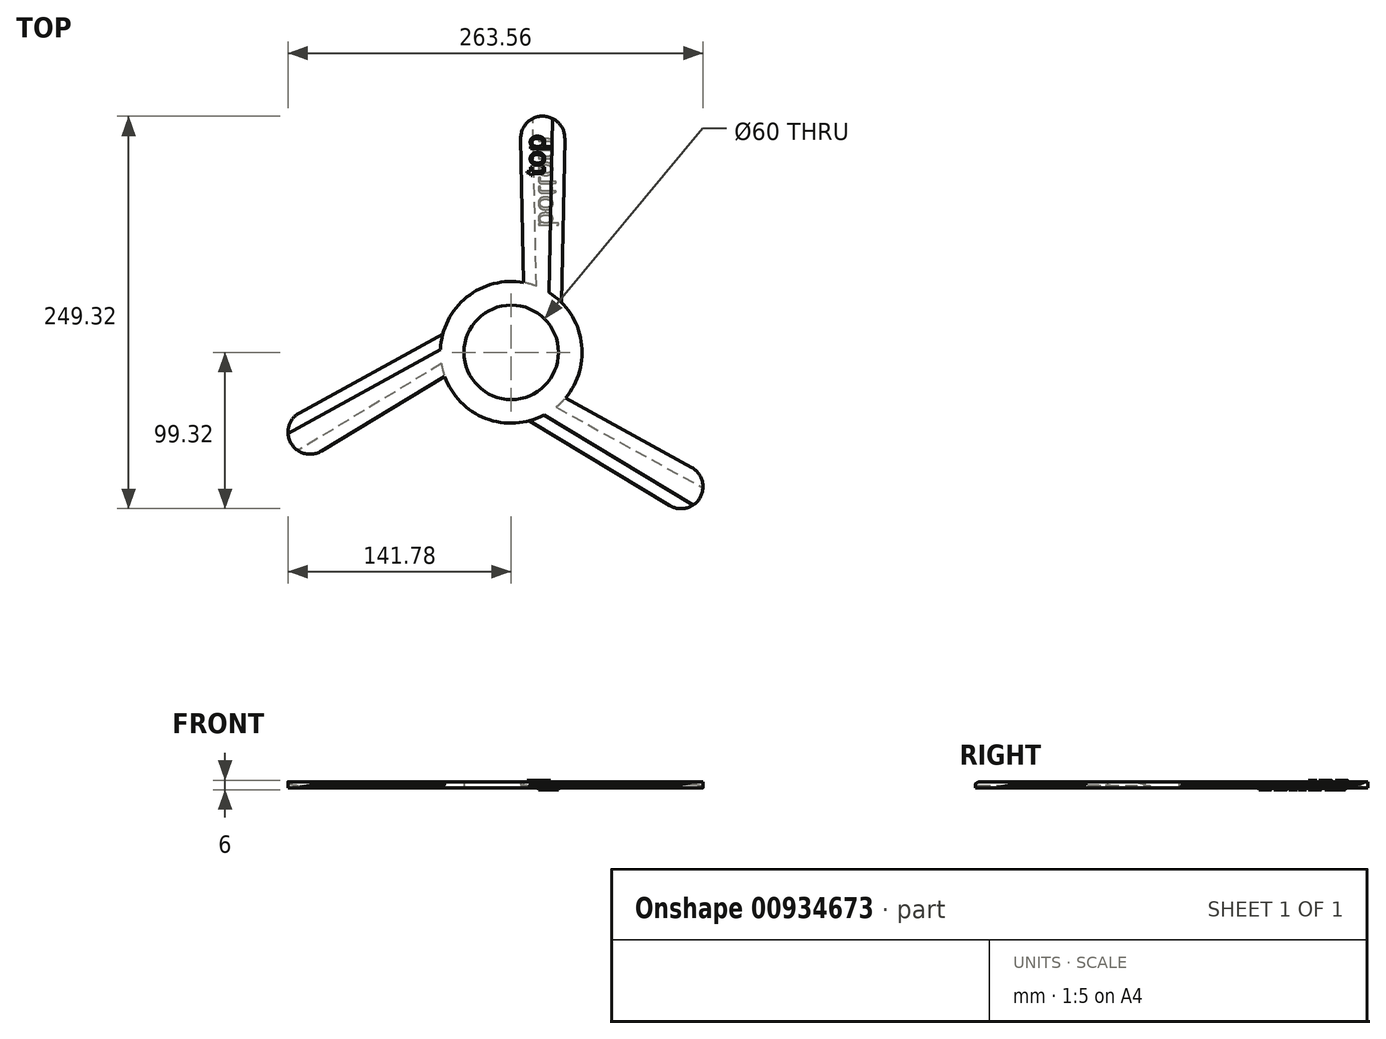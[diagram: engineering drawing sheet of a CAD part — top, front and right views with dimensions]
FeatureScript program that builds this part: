
annotation { "Feature Type Name" : "Feature", "Feature Type Description" : "" }
export const myFeature = defineFeature(function(context is Context, id is Id, definition is map)
    precondition{}
    {
        {
            var Q0;
            Q0=qCreatedBy(makeId("Top.planeOp"),FACE);
            var sketch = newSketch(context, id + "F0", { "sketchPlane" : qUnion([Q0])});
            skCircle(sketch, "E0", {"center": v(0, 0) * mm, "radius": 30 * mm});
            skArc(sketch, "E1", {"start": v(34.43, -28.97) * mm, "mid": v(44.96, 1.9) * mm, "end": v(31.87, 31.77) * mm});
            skLineSegment(sketch, "E2", {"start": v(0, 0) * mm, "end": v(0, 45) * mm, "construction": true});
            skLineSegment(sketch, "E3", {"start": v(6, 135.71) * mm, "end": v(7.87, 44.3) * mm});
            skLineSegment(sketch, "E4", {"start": v(34, 135.71) * mm, "end": v(31.87, 31.77) * mm});
            skLineSegment(sketch, "E5", {"start": v(20, 136) * mm, "end": v(20, 40.31) * mm, "construction": true});
            skArc(sketch, "E6", {"start": v(34, 135.71) * mm, "mid": v(20, 150) * mm, "end": v(6, 135.71) * mm});
            skLineSegment(sketch, "E7", {"start": v(0, 0) * mm, "end": v(45, 0) * mm, "construction": true});
            skArc(sketch, "E8.1.0", {"start": v(100.53, -97.3) * mm, "mid": v(119.9, -92.32) * mm, "end": v(114.53, -73.05) * mm});
            skLineSegment(sketch, "E8.1.1", {"start": v(100.53, -97.3) * mm, "end": v(11.58, -43.49) * mm});
            skLineSegment(sketch, "E8.1.2", {"start": v(107.78, -85.32) * mm, "end": v(24.91, -37.48) * mm, "construction": true});
            skLineSegment(sketch, "E8.1.3", {"start": v(114.53, -73.05) * mm, "end": v(34.43, -28.97) * mm});
            skArc(sketch, "E8.2.0", {"start": v(-134.53, -38.41) * mm, "mid": v(-139.9, -57.68) * mm, "end": v(-120.53, -62.66) * mm});
            skLineSegment(sketch, "E8.2.1", {"start": v(-134.53, -38.41) * mm, "end": v(-43.45, 11.72) * mm});
            skLineSegment(sketch, "E8.2.2", {"start": v(-127.78, -50.68) * mm, "end": v(-44.91, -2.84) * mm, "construction": true});
            skLineSegment(sketch, "E8.2.3", {"start": v(-120.53, -62.66) * mm, "end": v(-42.3, -15.34) * mm});
            skLineSegment(sketch, "E8.anchor1", {"start": v(0, 0) * mm, "end": v(7.87, 44.3) * mm, "construction": true});
            skLineSegment(sketch, "E8.anchor2", {"start": v(0, 0) * mm, "end": v(-42.3, -15.34) * mm, "construction": true});
            skArc(sketch, "E9.trimOffspring", {"start": v(-42.3, -15.34) * mm, "mid": v(-20.84, -39.89) * mm, "end": v(11.58, -43.49) * mm});
            skArc(sketch, "E10.trimOffspring", {"start": v(7.87, 44.3) * mm, "mid": v(-24.12, 37.99) * mm, "end": v(-43.45, 11.72) * mm});
            skSolve(sketch);
        }
        {
            var Q0;
            Q0=qSketchRegion(id+"F0",true);
            extrude(context, id + "F1", {"entities" : qUnion([Q0]), "depth" : 4 * mm, "offsetDistance" : 25 * mm});
        }
        {
            var Q0;
            Q0=makeQuery(id+"F1.opExtrude","CAP_EDGE",EDGE,{"disambiguationData":[OSD([sQuery(id+"F0.wireOp",EDGE,"E3")])],"isStart":true});
            var Q1;
            Q1=makeQuery(id+"F1.opExtrude","CAP_EDGE",EDGE,{"disambiguationData":[OSD([sQuery(id+"F0.wireOp",EDGE,"E8.1.3")])],"isStart":true});
            var Q2;
            Q2=makeQuery(id+"F1.opExtrude","CAP_EDGE",EDGE,{"disambiguationData":[OSD([sQuery(id+"F0.wireOp",EDGE,"E8.2.3")])],"isStart":true});
            var Q3;
            Q3=makeQuery(id+"F1.opExtrude","CAP_EDGE",EDGE,{"disambiguationData":[OSD([sQuery(id+"F0.wireOp",EDGE,"E8.1.1")])],"isStart":false});
            var Q4;
            Q4=makeQuery(id+"F1.opExtrude","CAP_EDGE",EDGE,{"disambiguationData":[OSD([sQuery(id+"F0.wireOp",EDGE,"E4")])],"isStart":false});
            var Q5;
            Q5=makeQuery(id+"F1.opExtrude","CAP_EDGE",EDGE,{"disambiguationData":[OSD([sQuery(id+"F0.wireOp",EDGE,"E8.2.1")])],"isStart":false});
            chamfer(context, id + "F2", {"entities" : qUnion([Q0, Q1, Q2, Q3, Q4, Q5]), "chamferType" : ChamferType.OFFSET_ANGLE, "width" : 8 * mm, "oppositeDirection" : true, "angle" : 15 * degree});
        }
        {
            var Q0;
            Q0=makeQuery(id+"F1.opExtrude","CAP_FACE",FACE,{"disambiguationData":[OSD([sQuery(id+"F0.wireOp",EDGE,"E0"),sQuery(id+"F0.wireOp",EDGE,"E1"),sQuery(id+"F0.wireOp",EDGE,"E3"),sQuery(id+"F0.wireOp",EDGE,"E4"),sQuery(id+"F0.wireOp",EDGE,"E6"),sQuery(id+"F0.wireOp",EDGE,"E8.1.0"),sQuery(id+"F0.wireOp",EDGE,"E8.1.1"),sQuery(id+"F0.wireOp",EDGE,"E8.1.3"),sQuery(id+"F0.wireOp",EDGE,"E8.2.0"),sQuery(id+"F0.wireOp",EDGE,"E8.2.1"),sQuery(id+"F0.wireOp",EDGE,"E8.2.3"),sQuery(id+"F0.wireOp",EDGE,"E9.trimOffspring"),sQuery(id+"F0.wireOp",EDGE,"E10.trimOffspring")])],"isStart":false});
            var sketch = newSketch(context, id + "F3", { "sketchPlane" : qUnion([Q0])});
            skText(sketch, "E11", { "text": "top", "fontName": "OpenSans-Regular.ttf"});
            const initialGuessF3  = {"E11": [0.0211, 0.11205, 0, 1, 0.012]};
            skSetInitialGuess(sketch, initialGuessF3);
            skSolve(sketch);
        }
        {
            var Q0;
            Q0=qSketchRegion(id+"F3",true);
            extrude(context, id + "F4", {"entities" : qUnion([Q0]), "operationType" : NewBodyOperationType.ADD, "depth" : 1 * mm, "offsetDistance" : 25 * mm});
        }
        {
            var Q0;
            Q0=makeQuery(id+"F1.opExtrude","CAP_FACE",FACE,{"disambiguationData":[OSD([sQuery(id+"F0.wireOp",EDGE,"E0"),sQuery(id+"F0.wireOp",EDGE,"E1"),sQuery(id+"F0.wireOp",EDGE,"E3"),sQuery(id+"F0.wireOp",EDGE,"E4"),sQuery(id+"F0.wireOp",EDGE,"E6"),sQuery(id+"F0.wireOp",EDGE,"E8.1.0"),sQuery(id+"F0.wireOp",EDGE,"E8.1.1"),sQuery(id+"F0.wireOp",EDGE,"E8.1.3"),sQuery(id+"F0.wireOp",EDGE,"E8.2.0"),sQuery(id+"F0.wireOp",EDGE,"E8.2.1"),sQuery(id+"F0.wireOp",EDGE,"E8.2.3"),sQuery(id+"F0.wireOp",EDGE,"E9.trimOffspring"),sQuery(id+"F0.wireOp",EDGE,"E10.trimOffspring")])],"isStart":true});
            var sketch = newSketch(context, id + "F5", { "sketchPlane" : qUnion([Q0])});
            skText(sketch, "E12", { "text": "bottom", "fontName": "OpenSans-Regular.ttf"});
            const initialGuessF5  = {"E12": [0.01735, -0.07937, 0, -1, 0.012]};
            skSetInitialGuess(sketch, initialGuessF5);
            skSolve(sketch);
        }
        {
            var Q0;
            Q0=qSketchRegion(id+"F5",true);
            extrude(context, id + "F6", {"entities" : qUnion([Q0]), "operationType" : NewBodyOperationType.ADD, "depth" : 1 * mm, "offsetDistance" : 25 * mm});
        }
    });
